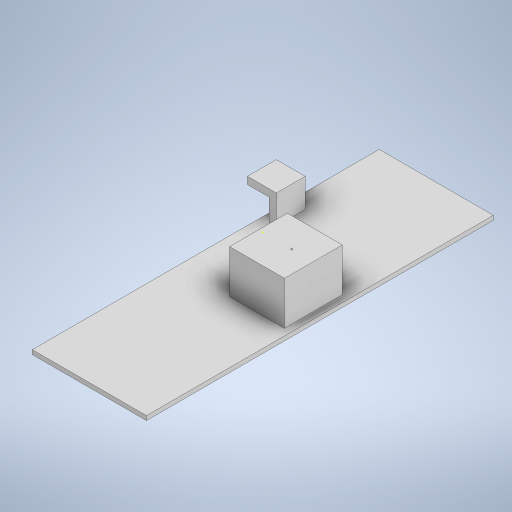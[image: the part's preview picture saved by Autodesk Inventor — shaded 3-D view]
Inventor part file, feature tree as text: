
AUTODESK INVENTOR PART (.ipt)
format: ipt  version: 2023 (Build 270158000, 158)  size: 305,664 bytes
history: native  units: mm
features: sketch x10, extrude x8
ambient origin geometry x8: Origin, YZ Plane, XZ Plane, XY Plane, X Axis, Y Axis, Z Axis, Center Point
bodies: Body1 (feature_tree)
feature tree (18):
  extrude  "Extrusion33"  Depth=240.0mm
  extrude  "Extrusion34"  Depth=3.0mm
  sketch  "Sketch46"  dims[d143=40.0mm d144=30.0mm d145=0.0mm]
  extrude  "Extrusion35"  Depth=30.0mm TaperAngle=0.0deg
  sketch  "Sketch48"  dims[d149=1.0mm d150=0.0mm d151=0.0mm]
  extrude  "Extrusion36"  Depth=30.0mm
  extrude  "Extrusion38"  TaperAngle=0.0deg  [1 undecoded]
  extrude  "Extrusion39"  Depth=15.0mm
  extrude  "Extrusion40"  Depth=3.0mm
  extrude  "Extrusion41"  Depth=20.0mm TaperAngle=0.0deg
  sketch  "Sketch44"  dims[d138=79.0mm d139=240.0mm]
  sketch  "Sketch45"  dims[d140=3.0mm d141=0.0mm d142=38.0mm]
  sketch  "Sketch47"  dims[d146=36.0mm d147=30.0mm d148=-2.617994mm]
  sketch  "Sketch49"  dims[d156=20.0mm d157=15.0mm]
  sketch  "Sketch58"  dims[d158=15.0mm d159=0.0mm d160=3.0mm]
  sketch  "Sketch59"  dims[d161=20.0mm d162=35.0mm d163=0.0mm]
  sketch  "Sketch60"  dims[d164=5.0mm]
  sketch  "Sketch61"  dims[d165=20.0mm d166=20.0mm d167=0.0mm d168=20.0mm d169=20.0mm d170=5.0mm d171=0.0mm d49=0.5mm d50=0.872665mm d51=0.5mm d52=0.872665mm d130=0.5mm d131=0.872665mm d132=0.5mm d133=0.872665mm]
note: 1 required parameter value undecoded (feature->parameter linkage not recoverable at this tier; creation-order binding heuristic only, values carry confidence <= 0.55)
